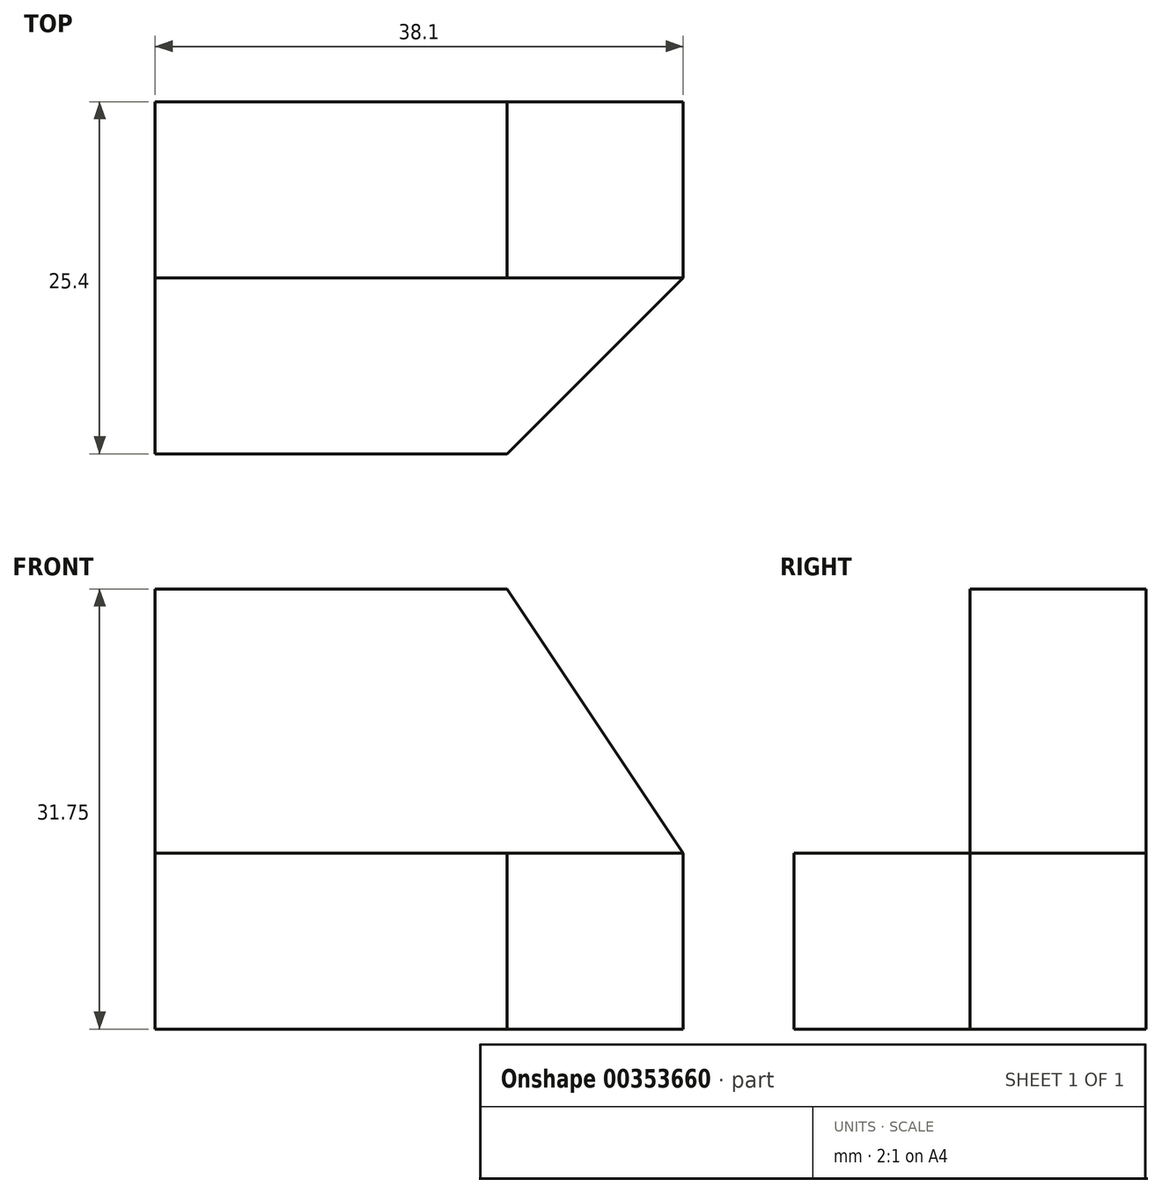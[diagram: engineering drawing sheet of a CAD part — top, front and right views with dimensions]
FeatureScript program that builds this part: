
annotation { "Feature Type Name" : "Feature", "Feature Type Description" : "" }
export const myFeature = defineFeature(function(context is Context, id is Id, definition is map)
    precondition{}
    {
        {
            var Q0;
            Q0=qCreatedBy(makeId("Right.planeOp"),FACE);
            var sketch = newSketch(context, id + "F0", { "sketchPlane" : qUnion([Q0])});
            skLineSegment(sketch, "E0", {"start": v(25.4, 31.75) * mm, "end": v(25.4, 0) * mm});
            skLineSegment(sketch, "E1", {"start": v(25.4, 0) * mm, "end": v(0, 0) * mm});
            skLineSegment(sketch, "E2", {"start": v(0, 0) * mm, "end": v(0, 12.7) * mm});
            skLineSegment(sketch, "E3", {"start": v(0, 12.7) * mm, "end": v(12.7, 12.7) * mm});
            skLineSegment(sketch, "E4", {"start": v(12.7, 12.7) * mm, "end": v(12.7, 31.75) * mm});
            skLineSegment(sketch, "E5", {"start": v(12.7, 31.75) * mm, "end": v(25.4, 31.75) * mm});
            skSolve(sketch);
        }
        {
            var Q0;
            Q0=makeQuery(id+"F0.imprint","IMPRINT",FACE,{"disambiguationData":[TD([[makeQuery(id+"F0.imprint","IMPRINT",EDGE,{"derivedFrom":sQuery(id+"F0.wireOp",EDGE,"E0")}),-1.0]])]});
            extrude(context, id + "F1", {"entities" : qUnion([Q0]), "depth" : 38.1 * mm});
        }
        {
            var Q0;
            Q0=makeQuery(id+"F1.opExtrude","SWEPT_FACE",FACE,{"disambiguationData":[OSD([sQuery(id+"F0.wireOp",EDGE,"E3")])]});
            var sketch = newSketch(context, id + "F2", { "sketchPlane" : qUnion([Q0])});
            skLineSegment(sketch, "E6", {"start": v(25.4, 0) * mm, "end": v(38.1, 12.7) * mm});
            skSolve(sketch);
        }
        {
            var Q0;
            {var subQ0=sQuery(id+"F2.wireOp",EDGE,"E6");Q0=makeQuery(id+"F2.imprint","IMPRINT",FACE,{"disambiguationData":[TD([[makeQuery(id+"F2.imprint","IMPRINT",EDGE,{"derivedFrom":subQ0}),-1.0]])]});}
            extrude(context, id + "F3", {"entities" : qUnion([Q0]), "operationType" : NewBodyOperationType.REMOVE, "oppositeDirection" : true, "depth" : 12.7 * mm});
        }
        {
            var Q0;
            Q0=makeQuery(id+"F1.opExtrude","SWEPT_FACE",FACE,{"disambiguationData":[OSD([sQuery(id+"F0.wireOp",EDGE,"E4")])]});
            var sketch = newSketch(context, id + "F4", { "sketchPlane" : qUnion([Q0])});
            skLineSegment(sketch, "E7", {"start": v(25.4, 31.75) * mm, "end": v(38.1, 12.7) * mm});
            skSolve(sketch);
        }
        {
            var Q0;
            {var subQ0=sQuery(id+"F4.wireOp",EDGE,"E7");Q0=makeQuery(id+"F4.imprint","IMPRINT",FACE,{"disambiguationData":[TD([[makeQuery(id+"F4.imprint","IMPRINT",EDGE,{"derivedFrom":subQ0}),1.0]])]});}
            extrude(context, id + "F5", {"entities" : qUnion([Q0]), "operationType" : NewBodyOperationType.REMOVE, "oppositeDirection" : true, "depth" : 12.7 * mm});
        }
    });
